# Revit family: PA_Арматура трубопроводов [редуктор давления с фильтром и манометром, VT.082.N] - VALTEC
name_source: partatom
category: Арматура трубопроводов
revit_build: Autodesk Revit 2018 (Build: 20180423_1000(x64)
units: mm (PartAtom-declared; Revit-internal decimal feet)

## family parameters
Всегда вертикально = Да
На основе рабочей плоскости = Нет
Общий = Нет
При загрузке вырезать с полостями = Нет
Размер круглого соединителя = Использовать диаметр
Тип детали = Вставляется

## types (1)
- VT.082.N
    ADSK_URL документации изделия = https://valtec.ru
    ADSK_URL страницы изделия = https://valtec.ru
    ADSK_Материал = Сталь, нержавеющая - VALTEC
    URL = https://valtec.ru
    n = 0 мм
    n1 = -7 мм
    n10 = -32 мм
    n11 = -34 мм
    n12 = -39 мм
    n13 = -40 мм
    n14 = -47 мм
    n15 = -48 мм
    n16 = -70 мм
    n2 = -7 мм
    n3 = -13 мм
    n4 = -14 мм
    n5 = -35 мм
    n6 = -14 мм
    n7 = -15 мм
    n8 = -23 мм
    n9 = -24 мм
    Изготовитель = VALTEC
    Материал доб.1 = Черный - VALTEC
    Материал доб.2 = Стекло
    Материал доб.3 = Латунь - VALTEC
    Таблица 1 = PA_Арматура трубопроводов [редуктор давления с фильтром и манометром, VT.082.N] - VALTEC - Таблица 1
    Таблица 2 = PA_Арматура трубопроводов [редуктор давления с фильтром и манометром, VT.082.N] - VALTEC - Таблица 2
